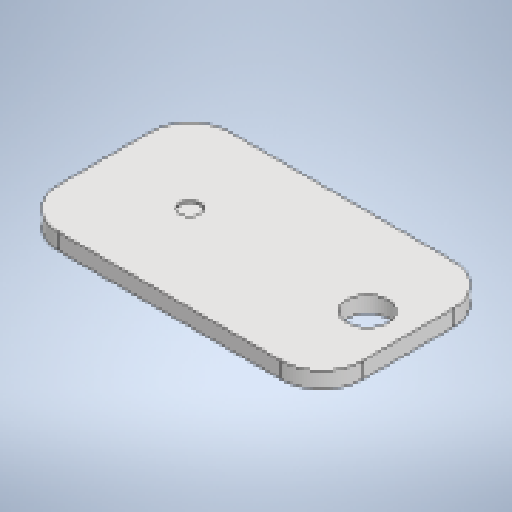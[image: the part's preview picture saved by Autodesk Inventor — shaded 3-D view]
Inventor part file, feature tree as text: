
AUTODESK INVENTOR PART (.ipt)
format: ipt  version: 2025.1 (Build 291241020, 241B)  size: 187,392 bytes
history: native  units: mm
features: sketch x2, other x2, sheet_metal_op x1, chamfer x1, extrude x1
ambient origin geometry x8: Origin, YZ Plane, XZ Plane, XY Plane, X Axis, Y Axis, Z Axis, Center Point
bodies: Solid1 (feature_tree)
feature tree (7):
  sheet_metal_op  "Face1"
  chamfer  "Corner Round1"
  extrude  "Extrusion2"  Depth=85.0mm
  sketch  "Sketch1"  dims[d0=150.0mm d1=85.0mm]
  other  "Plate1"
  sketch  "Sketch5"  dims[d2=8.0mm d22=5.0mm d23=20.0mm d25=20.0mm d26=20.0mm d27=10.0mm d28=1.0mm d29=0.0mm]
  other  "Definition1"
